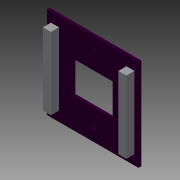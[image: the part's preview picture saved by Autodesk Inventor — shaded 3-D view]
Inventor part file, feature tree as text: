
AUTODESK INVENTOR PART (.ipt)
format: ipt  version: 2015 (Build 190159000, 159)  size: 140,288 bytes
history: native  units: in
note: dims shown in document units (in); Inventor stores cm internally (conversion verified against a paired STEP export)
features: extrude x2, sketch x2
ambient origin geometry x8: Origin, YZ Plane, XZ Plane, XY Plane, X Axis, Y Axis, Z Axis, Center Point
bodies: Solid1 (feature_tree)
feature tree (4):
  extrude  "Extrusion1"  Depth=2.25in
  extrude  "Extrusion4"  Depth=0.1in
  sketch  "Sketch1"  dims[d0=0.0646in d1=0.0in d2=2.25in]
  sketch  "Sketch4"  dims[d4=2.25in d21=0.1in d22=1.7717in d23=0.1969in d24=0.8858in d25=0.1969in d26=0.0in d27=0.1024in d28=0.15in d29=0.1024in d30=1.6535in d31=0.9843in d32=0.7874in]
